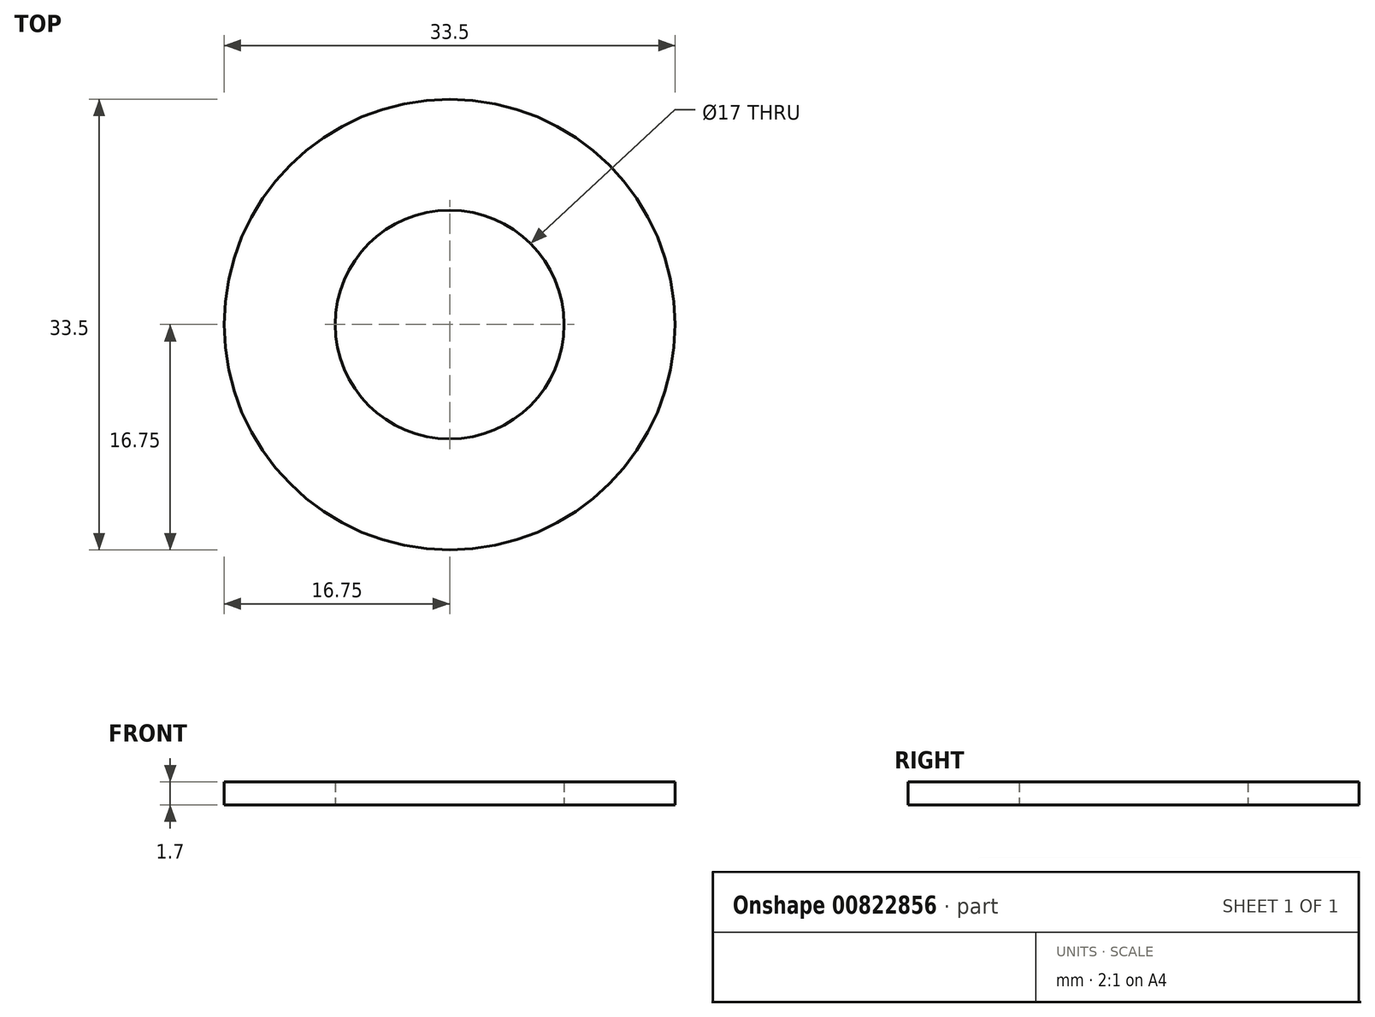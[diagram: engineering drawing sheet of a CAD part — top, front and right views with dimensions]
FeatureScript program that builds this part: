
annotation { "Feature Type Name" : "Feature", "Feature Type Description" : "" }
export const myFeature = defineFeature(function(context is Context, id is Id, definition is map)
    precondition{}
    {
        {
            var Q0;
            Q0=qCreatedBy(makeId("Top.planeOp"),FACE);
            var sketch = newSketch(context, id + "F0", { "sketchPlane" : qUnion([Q0])});
            skCircle(sketch, "E0", {"center": v(0, 0) * mm, "radius": 8.5 * mm});
            skCircle(sketch, "E1", {"center": v(0, 0) * mm, "radius": 16.75 * mm});
            skSolve(sketch);
        }
        {
            var Q0;
            Q0 = qSketchRegion(id + "F0", true);
            extrude(context, id + "F1", {"entities" : qUnion([Q0]), "depth" : 1.7 * mm, "offsetDistance" : 25 * mm});
        }
    });
